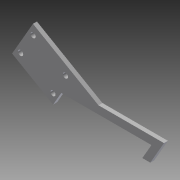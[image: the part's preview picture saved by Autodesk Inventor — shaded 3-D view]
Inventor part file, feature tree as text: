
AUTODESK INVENTOR PART (.ipt)
format: ipt  version: 2013 (Build 170138000, 138)  size: 110,592 bytes
history: native  units: in
note: dims shown in document units (in); Inventor stores cm internally (conversion verified against a paired STEP export)
features: extrude x1, sketch x1
ambient origin geometry x8: Origin, YZ Plane, XZ Plane, XY Plane, X Axis, Y Axis, Z Axis, Center Point
feature tree (2):
  extrude  "Extrusion2"  Depth=5.3671in
  sketch  "Sketch1"  dims[d14=0.5in d39=5.12in d41=1.0in d42=0.5in d43=60.0deg d44=60.0deg d45=0.5in d51=5.3671in d54=5.3671in d55=0.5in d56=2.62in d57=1.319in d58=1.319in d59=2.992in d60=1.6077in d61=0.315in d63=0.3268in d64=0.315in d66=0.327in d69=0.315in d70=0.5315in d72=0.327in d73=0.531in d74=0.315in d75=90.0deg d76=0.317in d77=0.25in d78=0.0in]
